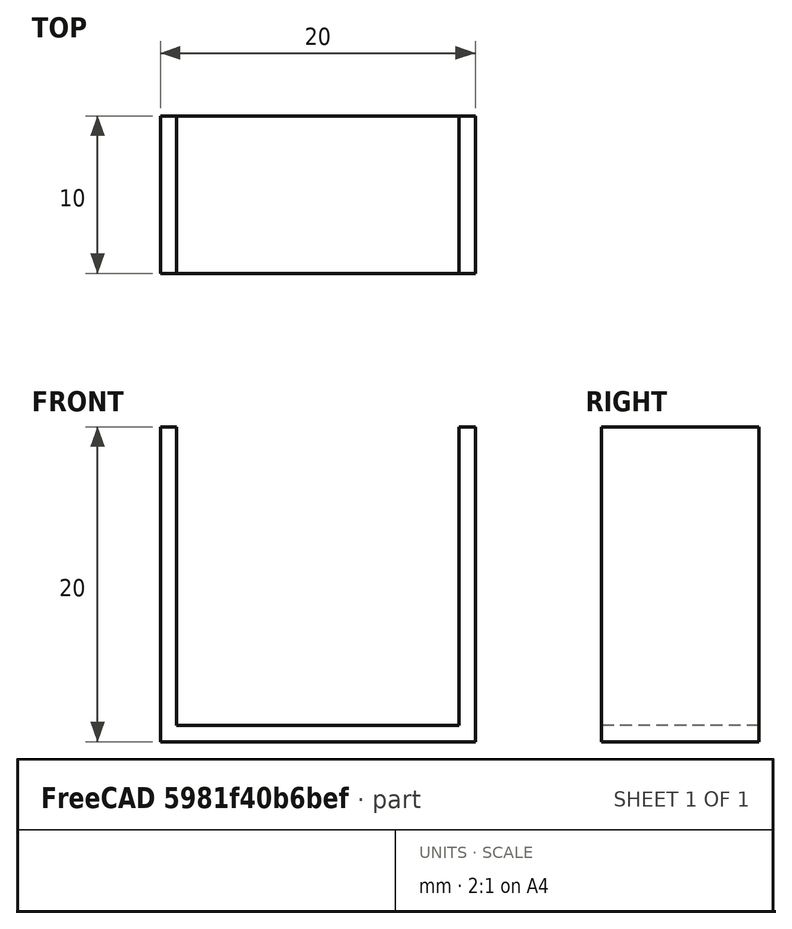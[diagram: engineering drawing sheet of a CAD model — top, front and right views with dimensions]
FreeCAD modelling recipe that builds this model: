
FCSTD DOCUMENT  (FreeCAD 1.1R14555 (Git shallow))
Label: Desk Protector
License: All rights reserved
LicenseURL: https://en.wikipedia.org/wiki/All_rights_reserved
objects: App::Point×1, Sketcher::SketchObject×1, PartDesign::Pad×1, PartDesign::Body×1
note: 6 computed .brp shape members not serialized (recipe doc carries the construction recipe); baked Part::Feature solids carry a one-line shape summary decoded from their .brp

FEATURE [App::Point] Origin001
  Role = Origin
FEATURE [Sketcher::SketchObject] Sketch
  ArcFitTolerance = 1e-06
  AttachmentSupport = -> [Origin]
  ExternalTypes = [0]
  FullyConstrained = false
  MakeInternals = false
  MapMode = 5
  Placement = pos=(0,0,0) rot=(1,0,0;1.5708rad)
  sketch-geometry (10):
    g0: LineSegment StartX=-8.975 StartY=8.975 StartZ=0 EndX=-8.975 EndY=-8.975 EndZ=0
    g1: LineSegment StartX=-8.975 StartY=-8.975 StartZ=0 EndX=8.975 EndY=-8.975 EndZ=0
    g2: LineSegment StartX=8.975 StartY=-8.975 StartZ=0 EndX=8.975 EndY=8.975 EndZ=0
    g3: LineSegment StartX=-10 StartY=10 StartZ=0 EndX=-10 EndY=-10 EndZ=0
    g4: LineSegment StartX=-10 StartY=-10 StartZ=0 EndX=10 EndY=-10 EndZ=0
    g5: LineSegment StartX=10 StartY=-10 StartZ=0 EndX=10 EndY=10 EndZ=0
    g6: LineSegment StartX=10 StartY=10 StartZ=0 EndX=8.975 EndY=10 EndZ=0
    g7: LineSegment StartX=8.975 StartY=8.975 StartZ=0 EndX=8.975 EndY=10 EndZ=0
    g8: LineSegment StartX=-8.975 StartY=8.975 StartZ=0 EndX=-8.975 EndY=10 EndZ=0
    g9: LineSegment StartX=-8.975 StartY=10 StartZ=0 EndX=-10 EndY=10 EndZ=0
  constraints (26):
    c: Coincident(g0,g1)
    c: Coincident(g1,g2)
    c: Vertical(g0)
    c: Vertical(g2)
    c: Horizontal(g1)
    c: DistanceX(g1,g1) = 17.95
    c: Symmetric(g0,g1,g-1)
    c: DistanceY(g0,g0) = 17.95
    c: Coincident(g3,g4)
    c: Coincident(g4,g5)
    c: Coincident(g5,g6)
    c: Coincident(g9,g3)
    c: Vertical(g3)
    c: Vertical(g5)
    c: Horizontal(g4)
    c: Symmetric(g4,g3,g-1)
    c: DistanceY(g5,g5) = 20
    c: DistanceX(g4,g4) = 20
    c: Coincident(g7,g2)
    c: Vertical(g7)
    c: Coincident(g8,g0)
    c: Vertical(g8)
    c: Horizontal(g6)
    c: Horizontal(g9)
    c: Coincident(g7,g6)
    c: Coincident(g8,g9)
FEATURE [PartDesign::Pad] Pad
  Direction = (0,-1,0)
  Length = 10
  Length2 = 10
  Profile = -> Sketch
  ReferenceAxis = -> Sketch [N_Axis]
  Refine = true
  SideType = 0
  Suppressed = false
  Type = 0
  Type2 = 0
FEATURE [PartDesign::Body] Body
  AllowCompound = true
  Group = -> [Sketch,Pad]
  Origin = -> Origin
  Tip = -> Pad
